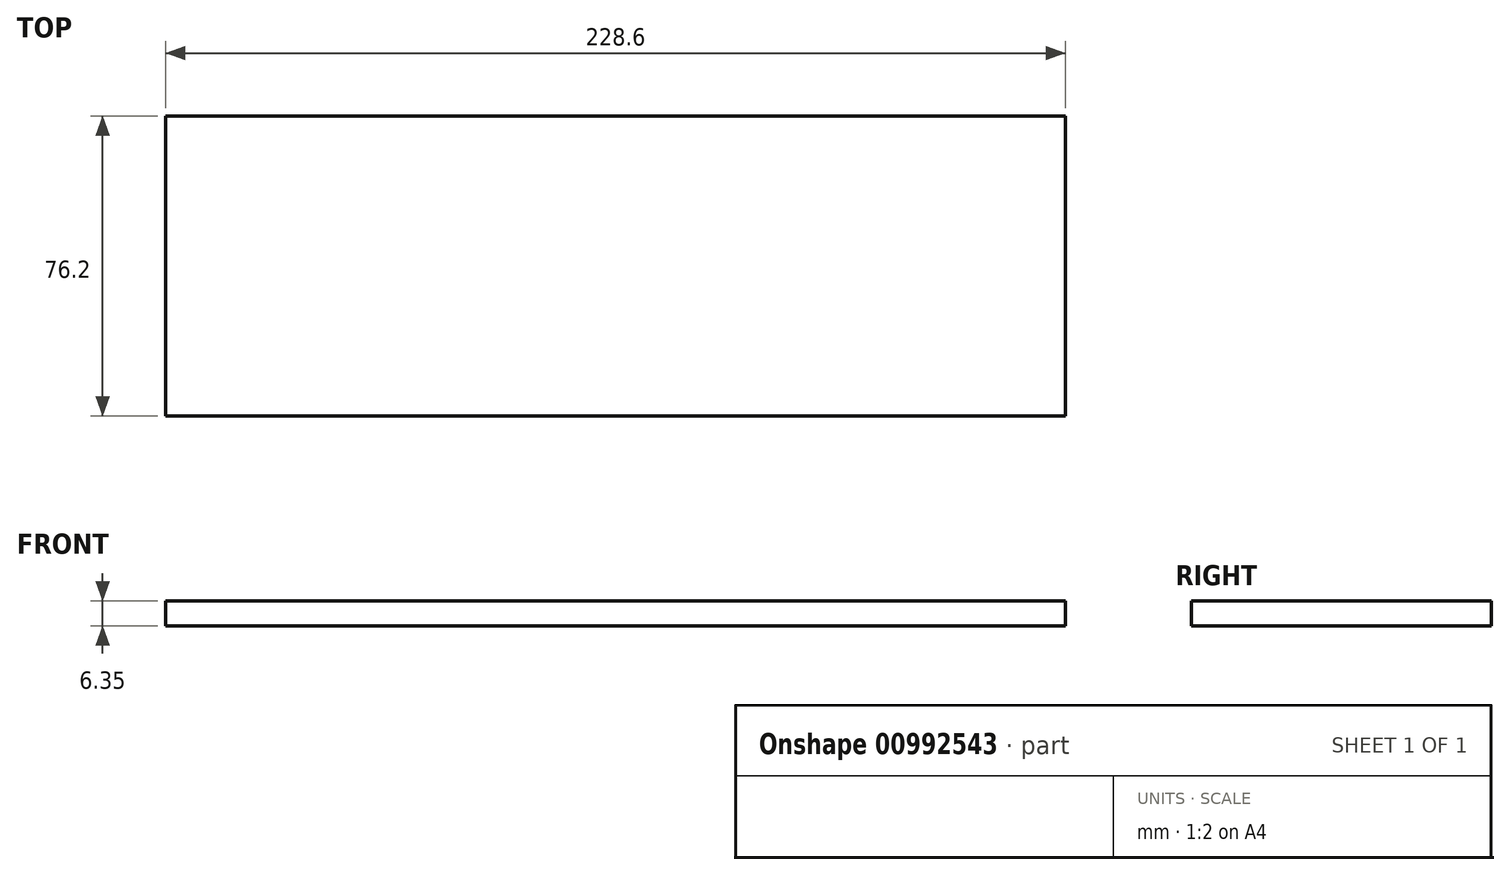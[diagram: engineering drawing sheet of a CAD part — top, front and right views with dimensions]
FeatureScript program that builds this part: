
annotation { "Feature Type Name" : "Feature", "Feature Type Description" : "" }
export const myFeature = defineFeature(function(context is Context, id is Id, definition is map)
    precondition{}
    {
        {
            var Q0;
            Q0=qCreatedBy(makeId("Top.planeOp"),FACE);
            var sketch = newSketch(context, id + "F0", { "sketchPlane" : qUnion([Q0])});
            skLineSegment(sketch, "E0.bottom", {"start": v(0, 0) * mm, "end": v(228.6, 0) * mm});
            skLineSegment(sketch, "E0.top", {"start": v(0, 76.2) * mm, "end": v(228.6, 76.2) * mm});
            skLineSegment(sketch, "E0.left", {"start": v(0, 0) * mm, "end": v(0, 76.2) * mm});
            skLineSegment(sketch, "E0.right", {"start": v(228.6, 0) * mm, "end": v(228.6, 76.2) * mm});
            skSolve(sketch);
        }
        {
            var Q0;
            Q0=makeQuery(id+"F0.imprint","IMPRINT",FACE,{"disambiguationData":[TD([[makeQuery(id+"F0.imprint","IMPRINT",EDGE,{"derivedFrom":sQuery(id+"F0.wireOp",EDGE,"E0.bottom")}),1.0]])]});
            extrude(context, id + "F1", {"entities" : qUnion([Q0]), "depth" : 6.35 * mm, "offsetDistance" : 25.4 * mm});
        }
    });
